# Revit family: Electronics_Communication_Talkaphone_AOR-120-Station-IP-Command-Unit
name_source: partatom
category: Telephone Devices
units: mm (PartAtom-declared; Revit-internal decimal feet)

## family parameters
Cut with Voids When Loaded = No
Host = Face
Maintain Annotation Orientation = No
OmniClass Number = 23.37.27.17
OmniClass Title = Emergency Call Equipment
Part Type = Normal
Room Calculation Point = No
Round Connector Dimension = Use Diameter
Shared = No

## types (1)
- 120-Station IP Command Unit
    AC Input Rating = 90 ~ 264 VAC, 50-60 Hz, 65W
    Apparent Load = 0 VA
    Assembly Code = D5030300
    Call Station Options = Indoor Flush Mount Model: AOR-IP-CSE-FM, Indoor Surface Mount Model: AOR-IP-CSE-SM
    Communication = IP Command Unit receives and selectively originates calls through built-in IP phone—providing an LCD and keys with LEDs to indicate IP Call Station line status (i.e. idle, ringing, or busy).
    Connection = RJ45 Ethernet
    Connectivity = Supports up to two (2) analog trunk (PSTN) lines or up to fifty (50) SIP trunk accounts (requires SIP service and Internet connectivity provided by others) for off-site communication
    Construction = 18 gauge, painted steel enclosure with acrylic window
    Default Elevation = 48.00 in
    Depth = 6.00 in
    Description = THE AOR-IP SERIES IS AN IP-BASED SYSTEM ACCOMMODATING UP TO 120 ADA-COMPLIANT AREA OF RESCUE IP CALL STATIONS. THE SYSTEM OFFERS CAPABILITY FOR MULTIPLE IP COMMAND UNITS, ON-AND OFF-PREMISE COMMUNICATION, AND IP NETWORK SUPERVISION
    Edition number = 1
    Environment = For indoor use
    Fault Monitoring = IP Supervisor (Model AOR-IP-SUP) automatically and continuously monitors for network pathway integrity for the AOR IP Stations and IP Command Unit(s). UPS Supervisor (Model AOR-IP-UPS-SUP) automatically and continuously monitors the primary power source being supplied to the uninterruptible power supply (UPS) for an IP Supervisor and either an IP Command Unit or an IP Auxiliary Command Unit.
    Height = 30.00 in
    Keynote = 27 30 00
    Manufacturer = Talkaphone
    Model = AOR-IP-120-CU
    Mounting = Flush mount with optional trim ring or surface mount
    Number of Poles = 1
    Power Factor = 1
    Power Source = 120VAC, 65W. IP Command Unit, IP Supervisor, and UPS Supervisor receive power from external UPS (120VAC).
    Product Guid = dbafcfe0-156d-4e50-8b9a-a2d47005f49f
    Product Material = Talkaphone - Steel - White
    Product data url = https://www.bimobject.com
    Programming = Programming and configuration through a web browser (web GUI). All programming is stored on non-volatile flash memory.
    Supervision Relay = IP Supervisor (Model AOR-IP-SUP) provides an SPST (Form 1A) output. UPS Supervisor (Model AOR-IP-UPS-SUP) provides a DPDT (Form C) output.
    URL = https://www.talkaphone.com
    Voltage = 120 V
    Warranty = 5-year limited warranty
    Width = 14.00 in
    Wiring = Minimum Cat5e. If required, fire resistive CI/CIC Ethernet cable is supported.

## geometry (parser evidence)
native form markers: Sweep x7
no freeform markers — native parametric forms only
